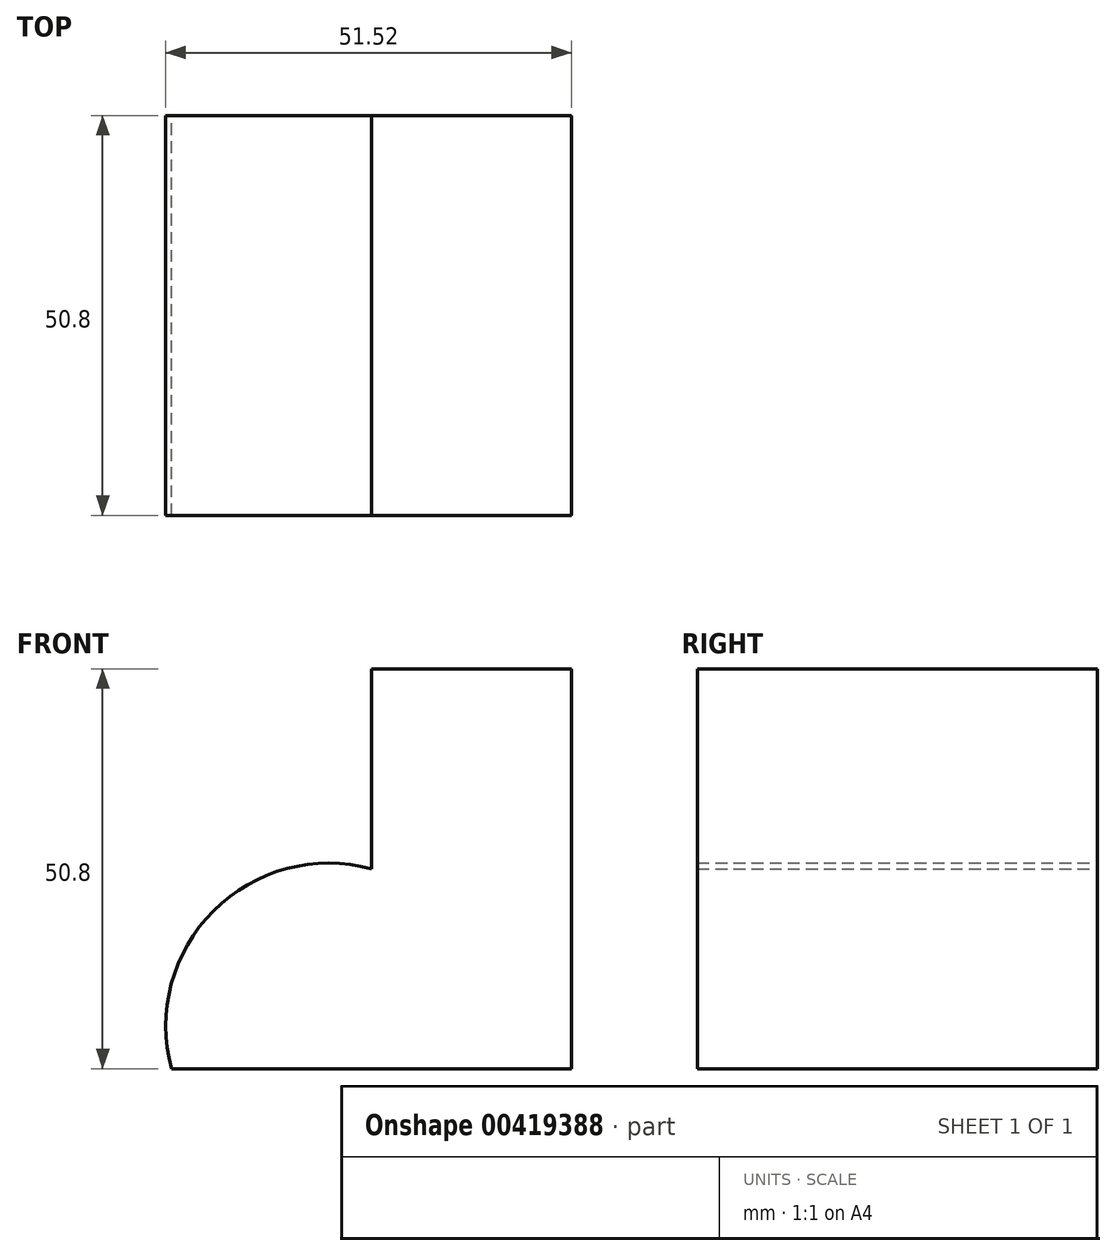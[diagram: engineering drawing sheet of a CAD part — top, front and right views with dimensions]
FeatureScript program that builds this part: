
annotation { "Feature Type Name" : "Feature", "Feature Type Description" : "" }
export const myFeature = defineFeature(function(context is Context, id is Id, definition is map)
    precondition{}
    {
        {
            var Q0;
            Q0=qCreatedBy(makeId("Front.planeOp"),FACE);
            var sketch = newSketch(context, id + "F0", { "sketchPlane" : qUnion([Q0])});
            skLineSegment(sketch, "E0", {"start": v(-39.72, 21.77) * mm, "end": v(-39.72, 47.17) * mm});
            skLineSegment(sketch, "E1", {"start": v(-39.72, 47.17) * mm, "end": v(-14.32, 47.17) * mm});
            skLineSegment(sketch, "E2", {"start": v(-14.32, 47.17) * mm, "end": v(-14.32, -3.63) * mm});
            skLineSegment(sketch, "E3", {"start": v(-14.32, -3.63) * mm, "end": v(-65.12, -3.63) * mm});
            skArc(sketch, "E4", {"start": v(-39.72, 21.77) * mm, "mid": v(-59.77, 16.42) * mm, "end": v(-65.12, -3.63) * mm});
            skSolve(sketch);
        }
        {
            var Q0;
            Q0 = qSketchRegion(id + "F0", true);
            extrude(context, id + "F1", {"entities" : qUnion([Q0]), "depth" : 50.8 * mm});
        }
    });
